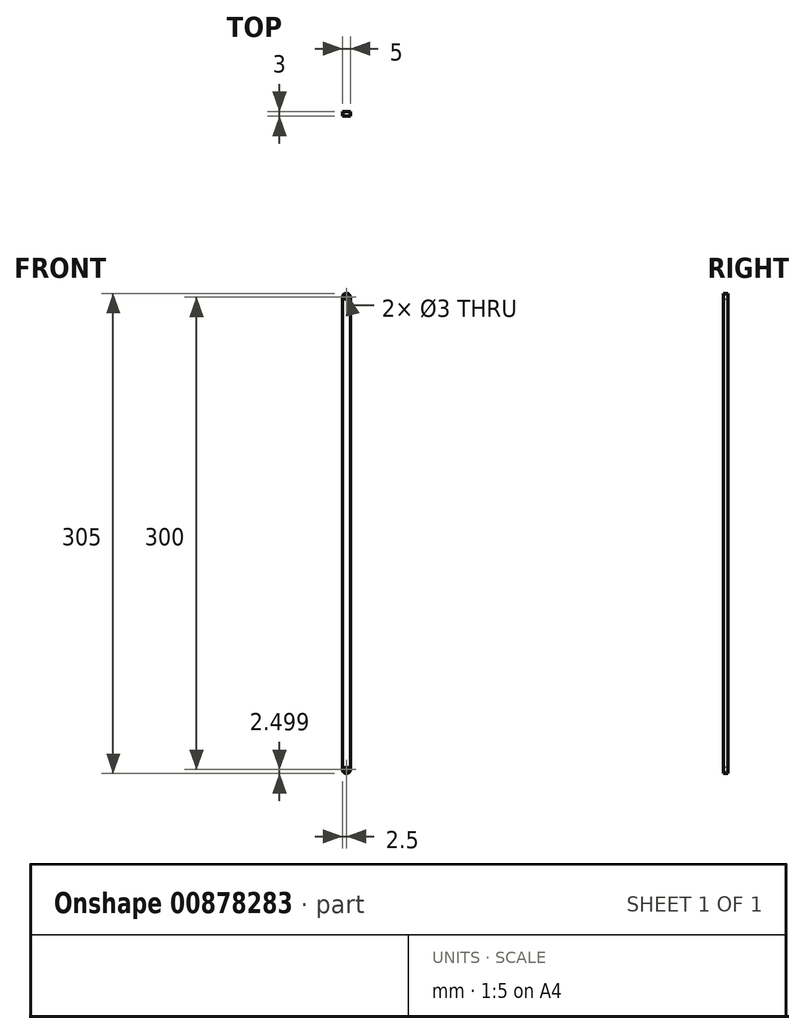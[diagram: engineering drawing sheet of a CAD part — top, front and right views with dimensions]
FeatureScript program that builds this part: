
annotation { "Feature Type Name" : "Feature", "Feature Type Description" : "" }
export const myFeature = defineFeature(function(context is Context, id is Id, definition is map)
    precondition{}
    {
        {
            var Q0;
            Q0=qCreatedBy(makeId("Front.planeOp"),FACE);
            var sketch = newSketch(context, id + "F0", { "sketchPlane" : qUnion([Q0])});
            skArc(sketch, "E0", {"start": v(2.5, 259.04) * mm, "mid": v(0, 261.54) * mm, "end": v(-2.5, 259.04) * mm});
            skArc(sketch, "E1", {"start": v(-2.5, -40.96) * mm, "mid": v(0, -43.46) * mm, "end": v(2.5, -40.96) * mm});
            skLineSegment(sketch, "E2", {"start": v(-2.5, 259.04) * mm, "end": v(-2.5, -40.96) * mm});
            skLineSegment(sketch, "E3", {"start": v(2.5, -40.96) * mm, "end": v(2.5, 259.04) * mm});
            skSolve(sketch);
        }
        {
            var Q0;
            Q0 = qSketchRegion(id + "F0", true);
            extrude(context, id + "F1", {"entities" : qUnion([Q0]), "depth" : 3 * mm, "offsetDistance" : 25 * mm});
        }
        {
            var Q0;
            Q0=makeQuery(id+"F1.opExtrude","CAP_FACE",FACE,{"disambiguationData":[OSD([sQuery(id+"F0.wireOp",EDGE,"E0"),sQuery(id+"F0.wireOp",EDGE,"E1"),sQuery(id+"F0.wireOp",EDGE,"E2"),sQuery(id+"F0.wireOp",EDGE,"E3")])],"isStart":false});
            var sketch = newSketch(context, id + "F2", { "sketchPlane" : qUnion([Q0])});
            skCircle(sketch, "E4", {"center": v(0, 259.04) * mm, "radius": 1.5 * mm});
            skCircle(sketch, "E5", {"center": v(0, -40.96) * mm, "radius": 1.5 * mm});
            skSolve(sketch);
        }
        {
            var Q0;
            Q0 = qSketchRegion(id + "F2", true);
            extrude(context, id + "F3", {"entities" : qUnion([Q0]), "operationType" : NewBodyOperationType.REMOVE, "endBound" : BoundingType.UP_TO_NEXT, "oppositeDirection" : true, "depth" : 25 * mm, "offsetDistance" : 25 * mm});
        }
    });
